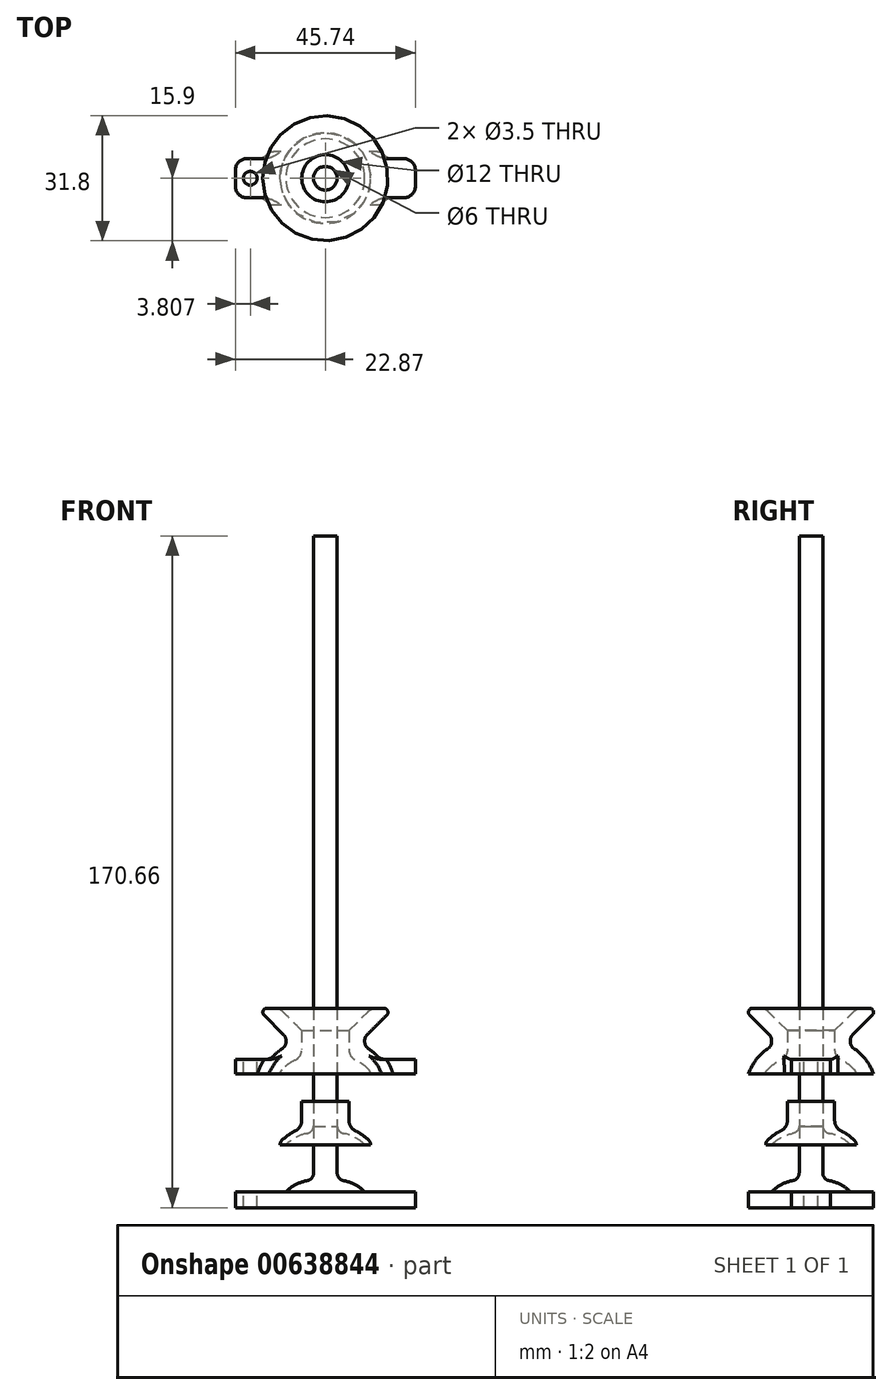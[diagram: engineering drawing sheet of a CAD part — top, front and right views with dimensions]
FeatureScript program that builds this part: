
annotation { "Feature Type Name" : "Feature", "Feature Type Description" : "" }
export const myFeature = defineFeature(function(context is Context, id is Id, definition is map)
    precondition{}
    {
        {
            var Q0;
            Q0=qCreatedBy(makeId("Front.planeOp"),FACE);
            var sketch = newSketch(context, id + "F0", { "sketchPlane" : qUnion([Q0])});
            skLineSegment(sketch, "E0", {"start": v(0, 0) * mm, "end": v(-3, 0) * mm, "construction": true});
            skLineSegment(sketch, "E1", {"start": v(-3, 1.83) * mm, "end": v(-3, 8) * mm});
            skPoint(sketch, "E2.endSnap0", {"position": v(-1.5, 0) * mm});
            skLineSegment(sketch, "E3", {"start": v(-3, 0) * mm, "end": v(-3, -3) * mm, "construction": true});
            skLineSegment(sketch, "E4", {"start": v(0, -3) * mm, "end": v(-10, -3) * mm, "construction": true});
            skArc(sketch, "E5", {"start": v(-4.66, -0.14) * mm, "mid": v(-7.56, -1.14) * mm, "end": v(-10, -3) * mm});
            skLineSegment(sketch, "E6", {"start": v(-3, 8) * mm, "end": v(-6, 8) * mm});
            skLineSegment(sketch, "E7", {"start": v(0, -3) * mm, "end": v(0, 8.98) * mm, "construction": true});
            skPoint(sketch, "E8.visualSharp", {"position": v(-11.5, -3) * mm});
            skPoint(sketch, "E9.visualSharp", {"position": v(-3, 0) * mm});
            skArc(sketch, "E9.filletArc", {"start": v(-4.66, -0.14) * mm, "mid": v(-3.47, 0.54) * mm, "end": v(-3, 1.83) * mm});
            skPoint(sketch, "E10.visualSharp", {"position": v(-10, -2.36) * mm});
            skArc(sketch, "E11.2", {"start": v(-7.73, 0.45) * mm, "mid": v(-9.52, -0.6) * mm, "end": v(-11.09, -1.97) * mm});
            skLineSegment(sketch, "E12", {"start": v(-6, 8) * mm, "end": v(-6, 3.17) * mm});
            skLineSegment(sketch, "E13", {"start": v(-10, -3) * mm, "end": v(-11.5, -3) * mm});
            skArc(sketch, "E14", {"start": v(-11.09, -1.97) * mm, "mid": v(-11.4, -2.44) * mm, "end": v(-11.5, -3) * mm});
            skPoint(sketch, "E15.visualSharp", {"position": v(-6, 1.09) * mm});
            skArc(sketch, "E15.filletArc", {"start": v(-7.73, 0.45) * mm, "mid": v(-6.47, 1.56) * mm, "end": v(-6, 3.17) * mm});
            skSolve(sketch);
        }
        {
            var Q0;
            Q0=makeQuery(id+"F0.imprint","IMPRINT",FACE,{"disambiguationData":[TD([[makeQuery(id+"F0.imprint","IMPRINT",EDGE,{"derivedFrom":sQuery(id+"F0.wireOp",EDGE,"E1")}),1.0]])]});
            var Q1;
            Q1=sQuery(id+"F0.wireOp",EDGE,"E7");
            revolve(context, id + "F1", {"entities" : qUnion([Q0]), "axis" : qUnion([Q1]), "revolveType" : RevolveType.FULL});
        }
        {
            var Q0;
            Q0=qCreatedBy(makeId("Front.planeOp"),FACE);
            var sketch = newSketch(context, id + "F2", { "sketchPlane" : qUnion([Q0])});
            skArc(sketch, "E16.0", {"start": v(-10.9, 3.44) * mm, "mid": v(-13.9, 0.63) * mm, "end": v(-15.84, -3) * mm});
            skLineSegment(sketch, "E16.1", {"start": v(-10, 5.51) * mm, "end": v(-10, 5.1) * mm});
            skLineSegment(sketch, "E17.0", {"start": v(-3, 1.83) * mm, "end": v(-3, 8) * mm});
            skArc(sketch, "E17.1", {"start": v(-4.66, -0.14) * mm, "mid": v(-7.56, -1.14) * mm, "end": v(-10, -3) * mm});
            skArc(sketch, "E18.0", {"start": v(-4.66, -0.14) * mm, "mid": v(-3.47, 0.54) * mm, "end": v(-3, 1.83) * mm});
            skLineSegment(sketch, "E19", {"start": v(-15.84, -3) * mm, "end": v(-15.84, -7) * mm});
            skLineSegment(sketch, "E20", {"start": v(-15.84, -7) * mm, "end": v(0, -7) * mm});
            skLineSegment(sketch, "E21", {"start": v(0, -7) * mm, "end": v(0, 8) * mm});
            skLineSegment(sketch, "E22", {"start": v(0, 8) * mm, "end": v(-3, 8) * mm});
            skLineSegment(sketch, "E23", {"start": v(-15.84, -3) * mm, "end": v(-15.84, 0.67) * mm, "construction": true});
            skLineSegment(sketch, "E24", {"start": v(-13.87, 0.67) * mm, "end": v(-25.87, 0.67) * mm});
            skLineSegment(sketch, "E25", {"start": v(-25.87, 0.67) * mm, "end": v(-25.87, -3) * mm});
            skLineSegment(sketch, "E26", {"start": v(-25.87, -3) * mm, "end": v(-15.84, -3) * mm});
            skLineSegment(sketch, "E27", {"start": v(-15.84, -7) * mm, "end": v(-25.87, -7) * mm});
            skLineSegment(sketch, "E28", {"start": v(-25.87, -7) * mm, "end": v(-25.87, -3) * mm});
            skLineSegment(sketch, "E29", {"start": v(-6, 8) * mm, "end": v(-11.66, 13.66) * mm});
            skLineSegment(sketch, "E30", {"start": v(-11.66, 13.66) * mm, "end": v(-17.31, 13.66) * mm});
            skLineSegment(sketch, "E31.trimOffspring", {"start": v(-10.59, 6.93) * mm, "end": v(-17.31, 13.66) * mm});
            skPoint(sketch, "E32.visualSharp", {"position": v(-10, 6.34) * mm});
            skArc(sketch, "E32.filletArc", {"start": v(-10, 5.51) * mm, "mid": v(-10.15, 6.28) * mm, "end": v(-10.59, 6.93) * mm});
            skPoint(sketch, "E33.visualSharp", {"position": v(-7.5, 3.98) * mm});
            skArc(sketch, "E33.filletArc", {"start": v(-10.9, 3.44) * mm, "mid": v(-10.24, 4.16) * mm, "end": v(-10, 5.1) * mm});
            skLineSegment(sketch, "E34", {"start": v(0, 8) * mm, "end": v(0, 13.66) * mm});
            skLineSegment(sketch, "E35", {"start": v(0, 13.66) * mm, "end": v(-3, 13.66) * mm});
            skLineSegment(sketch, "E36", {"start": v(-3, 13.66) * mm, "end": v(-3, 8) * mm});
            skArc(sketch, "E37.0", {"start": v(-11.09, -1.97) * mm, "mid": v(-11.4, -2.44) * mm, "end": v(-11.5, -3) * mm});
            skArc(sketch, "E37.1", {"start": v(-7.73, 0.45) * mm, "mid": v(-9.52, -0.6) * mm, "end": v(-11.09, -1.97) * mm});
            skArc(sketch, "E37.2", {"start": v(-7.73, 0.45) * mm, "mid": v(-6.47, 1.56) * mm, "end": v(-6, 3.17) * mm});
            skLineSegment(sketch, "E37.3", {"start": v(-6, 8) * mm, "end": v(-6, 3.17) * mm});
            skLineSegment(sketch, "E37.4", {"start": v(-10, -3) * mm, "end": v(-11.5, -3) * mm});
            skLineSegment(sketch, "E38", {"start": v(-11.5, -3) * mm, "end": v(-15.84, -3) * mm});
            skSolve(sketch);
        }
        {
            var Q0;
            Q0=makeQuery(id+"F2.imprint","IMPRINT",FACE,{"disambiguationData":[TD([[makeQuery(id+"F2.imprint","IMPRINT",EDGE,{"derivedFrom":sQuery(id+"F2.wireOp",EDGE,"E16.1")}),1.0]])]});
            var Q1;
            Q1=sQuery(id+"F0.wireOp",EDGE,"E7");
            revolve(context, id + "F3", {"surfaceOperationType" : NewSurfaceOperationType.NEW, "entities" : qUnion([Q0]), "axis" : qUnion([Q1]), "revolveType" : RevolveType.FULL});
        }
        {
            var Q0;
            Q0=makeQuery(id+"F2.imprint","IMPRINT",FACE,{"disambiguationData":[TD([[makeQuery(id+"F2.imprint","IMPRINT",EDGE,{"derivedFrom":sQuery(id+"F2.wireOp",EDGE,"E17.0")}),-1.0]])]});
            var Q1;
            Q1=makeQuery(id+"F2.imprint","IMPRINT",FACE,{"disambiguationData":[TD([[makeQuery(id+"F2.imprint","IMPRINT",EDGE,{"derivedFrom":sQuery(id+"F2.wireOp",EDGE,"E22")}),-1.0]])]});
            var Q2;
            Q2=sQuery(id+"F0.wireOp",EDGE,"E7");
            revolve(context, id + "F4", {"entities" : qUnion([Q0, Q1]), "axis" : qUnion([Q2]), "revolveType" : RevolveType.FULL});
        }
        {
            var Q0;
            {var subQ2=sQuery(id+"F2.wireOp",EDGE,"E24");Q0=makeQuery(id+"F2.imprint","IMPRINT",FACE,{"disambiguationData":[TD([[makeQuery(id+"F2.imprint","IMPRINT",EDGE,{"derivedFrom":subQ2}),1.0]])]});}
            extrude(context, id + "F5", {"entities" : qUnion([Q0]), "endBound" : BoundingType.SYMMETRIC, "depth" : 10 * mm, "offsetDistance" : 25 * mm});
        }
        {
            var Q0;
            Q0=makeQuery(id+"F2.imprint","IMPRINT",FACE,{"disambiguationData":[TD([[makeQuery(id+"F2.imprint","IMPRINT",EDGE,{"derivedFrom":sQuery(id+"F2.wireOp",EDGE,"E19")}),-1.0]])]});
            extrude(context, id + "F6", {"entities" : qUnion([Q0]), "endBound" : BoundingType.SYMMETRIC, "depth" : 10 * mm, "offsetDistance" : 25 * mm});
        }
        {
            var Q0;
            Q0=makeQuery(id+"F5.opExtrude","SWEPT_BODY",BODY,{"disambiguationData":[OSD([sQuery(id+"F2.wireOp",EDGE,"E16.0"),sQuery(id+"F2.wireOp",EDGE,"E24"),sQuery(id+"F2.wireOp",EDGE,"E25"),sQuery(id+"F2.wireOp",EDGE,"E26")])]});
            var Q1;
            Q1=makeQuery(id+"F6.opExtrude","SWEPT_BODY",BODY,{"disambiguationData":[OSD([sQuery(id+"F2.wireOp",EDGE,"E19"),sQuery(id+"F2.wireOp",EDGE,"E26"),sQuery(id+"F2.wireOp",EDGE,"E27"),sQuery(id+"F2.wireOp",EDGE,"E28")])]});
            transform(context, id + "F7", {"entities" : qUnion([Q0, Q1]), "transformType" : TransformType.TRANSLATION_3D, "dx" : 3 * mm, "dy" : 0 * mm, "dz" : 0 * mm, "makeCopy" : false});
        }
        {
            var Q0;
            Q0=makeQuery(id+"F5.opExtrude","SWEPT_BODY",BODY,{"disambiguationData":[OSD([sQuery(id+"F2.wireOp",EDGE,"E16.0"),sQuery(id+"F2.wireOp",EDGE,"E24"),sQuery(id+"F2.wireOp",EDGE,"E25"),sQuery(id+"F2.wireOp",EDGE,"E26")])]});
            var Q1;
            Q1=makeQuery(id+"F6.opExtrude","SWEPT_BODY",BODY,{"disambiguationData":[OSD([sQuery(id+"F2.wireOp",EDGE,"E19"),sQuery(id+"F2.wireOp",EDGE,"E26"),sQuery(id+"F2.wireOp",EDGE,"E27"),sQuery(id+"F2.wireOp",EDGE,"E28")])]});
            var Q2;
            Q2=qCreatedBy(makeId("Right.planeOp"),FACE);
            mirror(context, id + "F8", {"entities" : qUnion([Q0, Q1]), "mirrorPlane" : qUnion([Q2])});
        }
        {
            var Q0;
            Q0=makeQuery(id+"F5.opExtrude","SWEPT_BODY",BODY,{"disambiguationData":[OSD([sQuery(id+"F2.wireOp",EDGE,"E16.0"),sQuery(id+"F2.wireOp",EDGE,"E24"),sQuery(id+"F2.wireOp",EDGE,"E25"),sQuery(id+"F2.wireOp",EDGE,"E26")])]});
            var Q1;
            Q1=makeQuery(id+"F8.opPattern","COPY",BODY,{"derivedFrom":makeQuery(id+"F5.opExtrude","SWEPT_BODY",BODY,{"disambiguationData":[OSD([sQuery(id+"F2.wireOp",EDGE,"E16.0"),sQuery(id+"F2.wireOp",EDGE,"E24"),sQuery(id+"F2.wireOp",EDGE,"E25"),sQuery(id+"F2.wireOp",EDGE,"E26")])]}),"instanceName":"1"});
            var Q2;
            Q2=makeQuery(id+"F3.opRevolve","SWEPT_BODY",BODY,{"disambiguationData":[OSD([sQuery(id+"F2.wireOp",EDGE,"bc18d605-b98b-438b-80f2-28af09894532.0"),sQuery(id+"F2.wireOp",EDGE,"bc18d605-b98b-438b-80f2-28af09894532.1"),sQuery(id+"F2.wireOp",EDGE,"E16.0"),sQuery(id+"F2.wireOp",EDGE,"E16.1"),sQuery(id+"F2.wireOp",EDGE,"e265a185-1811-4eb8-86b9-4855075399bd.0"),sQuery(id+"F2.wireOp",EDGE,"0085ed8a-558a-43ff-81f7-92fb0c2dc086.0"),sQuery(id+"F2.wireOp",EDGE,"H8TFnSOD-seKw-8r3j-Luj8-icW1VKLXzKkm"),sQuery(id+"F2.wireOp",EDGE,"E29"),sQuery(id+"F2.wireOp",EDGE,"E30"),sQuery(id+"F2.wireOp",EDGE,"E31.trimOffspring"),sQuery(id+"F2.wireOp",EDGE,"E32.filletArc"),sQuery(id+"F2.wireOp",EDGE,"E33.filletArc")])]});
            booleanBodies(context, id + "F9", {"operationType" : BooleanOperationType.UNION, "tools" : qUnion([Q0, Q1, Q2])});
        }
        {
            var Q0;
            Q0=makeQuery(id+"F6.opExtrude","SWEPT_BODY",BODY,{"disambiguationData":[OSD([sQuery(id+"F2.wireOp",EDGE,"E19"),sQuery(id+"F2.wireOp",EDGE,"E26"),sQuery(id+"F2.wireOp",EDGE,"E27"),sQuery(id+"F2.wireOp",EDGE,"E28")])]});
            var Q1;
            Q1=makeQuery(id+"F4.opRevolve","SWEPT_BODY",BODY,{"disambiguationData":[OSD([sQuery(id+"F2.wireOp",EDGE,"E17.0"),sQuery(id+"F2.wireOp",EDGE,"E17.1"),sQuery(id+"F2.wireOp",EDGE,"E17.2"),sQuery(id+"F2.wireOp",EDGE,"E18.0"),sQuery(id+"F2.wireOp",EDGE,"H8TFnSOD-seKw-8r3j-Luj8-icW1VKLXzKkm"),sQuery(id+"F2.wireOp",EDGE,"E19"),sQuery(id+"F2.wireOp",EDGE,"E20"),sQuery(id+"F2.wireOp",EDGE,"E21"),sQuery(id+"F2.wireOp",EDGE,"E34"),sQuery(id+"F2.wireOp",EDGE,"E35"),sQuery(id+"F2.wireOp",EDGE,"E36")])]});
            var Q2;
            Q2=makeQuery(id+"F8.opPattern","COPY",BODY,{"derivedFrom":makeQuery(id+"F6.opExtrude","SWEPT_BODY",BODY,{"disambiguationData":[OSD([sQuery(id+"F2.wireOp",EDGE,"E19"),sQuery(id+"F2.wireOp",EDGE,"E26"),sQuery(id+"F2.wireOp",EDGE,"E27"),sQuery(id+"F2.wireOp",EDGE,"E28")])]}),"instanceName":"1"});
            booleanBodies(context, id + "F10", {"operationType" : BooleanOperationType.UNION, "tools" : qUnion([Q0, Q1, Q2])});
        }
        {
            var Q0;
            Q0=makeQuery(id+"F8.opPattern","COPY",EDGE,{"derivedFrom":makeQuery(id+"F5.opExtrude","CAP_EDGE",EDGE,{"disambiguationData":[OSD([sQuery(id+"F2.wireOp",EDGE,"E25")])],"isStart":false}),"instanceName":"1"});
            var Q1;
            Q1=makeQuery(id+"F8.opPattern","COPY",EDGE,{"derivedFrom":makeQuery(id+"F5.opExtrude","CAP_EDGE",EDGE,{"disambiguationData":[OSD([sQuery(id+"F2.wireOp",EDGE,"E25")])],"isStart":true}),"instanceName":"1"});
            var Q2;
            Q2=makeQuery(id+"F8.opPattern","COPY",EDGE,{"derivedFrom":makeQuery(id+"F6.opExtrude","CAP_EDGE",EDGE,{"disambiguationData":[OSD([sQuery(id+"F2.wireOp",EDGE,"E28")])],"isStart":true}),"instanceName":"1"});
            var Q3;
            Q3=makeQuery(id+"F8.opPattern","COPY",EDGE,{"derivedFrom":makeQuery(id+"F6.opExtrude","CAP_EDGE",EDGE,{"disambiguationData":[OSD([sQuery(id+"F2.wireOp",EDGE,"E28")])],"isStart":false}),"instanceName":"1"});
            var Q4;
            {var subQ0=sQuery(id+"F2.wireOp",EDGE,"E19");Q4=makeQuery(id+"F10.opBoolean","INTERSECT",EDGE,{"derivedFrom":[makeQuery(id+"F4.opRevolve","SWEPT_FACE",FACE,{"disambiguationData":[OSD([subQ0])]}),makeQuery(id+"F8.opPattern","COPY",FACE,{"derivedFrom":makeQuery(id+"F6.opExtrude","CAP_FACE",FACE,{"disambiguationData":[OSD([subQ0,sQuery(id+"F2.wireOp",EDGE,"E26"),sQuery(id+"F2.wireOp",EDGE,"E27"),sQuery(id+"F2.wireOp",EDGE,"E28")])],"isStart":false}),"instanceName":"1"})]});}
            var Q5;
            {var subQ0=sQuery(id+"F2.wireOp",EDGE,"E19");Q5=makeQuery(id+"F10.opBoolean","INTERSECT",EDGE,{"derivedFrom":[makeQuery(id+"F4.opRevolve","SWEPT_FACE",FACE,{"disambiguationData":[OSD([subQ0])]}),makeQuery(id+"F8.opPattern","COPY",FACE,{"derivedFrom":makeQuery(id+"F6.opExtrude","CAP_FACE",FACE,{"disambiguationData":[OSD([subQ0,sQuery(id+"F2.wireOp",EDGE,"E26"),sQuery(id+"F2.wireOp",EDGE,"E27"),sQuery(id+"F2.wireOp",EDGE,"E28")])],"isStart":true}),"instanceName":"1"})]});}
            var Q6;
            {var subQ0=sQuery(id+"F2.wireOp",EDGE,"E19");Q6=makeQuery(id+"F10.opBoolean","INTERSECT",EDGE,{"derivedFrom":[makeQuery(id+"F4.opRevolve","SWEPT_FACE",FACE,{"disambiguationData":[OSD([subQ0])]}),makeQuery(id+"F6.opExtrude","CAP_FACE",FACE,{"disambiguationData":[OSD([subQ0,sQuery(id+"F2.wireOp",EDGE,"E26"),sQuery(id+"F2.wireOp",EDGE,"E27"),sQuery(id+"F2.wireOp",EDGE,"E28")])],"isStart":false})]});}
            var Q7;
            Q7=makeQuery(id+"F6.opExtrude","CAP_EDGE",EDGE,{"disambiguationData":[OSD([sQuery(id+"F2.wireOp",EDGE,"E28")])],"isStart":false});
            var Q8;
            Q8=makeQuery(id+"F5.opExtrude","CAP_EDGE",EDGE,{"disambiguationData":[OSD([sQuery(id+"F2.wireOp",EDGE,"E25")])],"isStart":false});
            var Q9;
            Q9=makeQuery(id+"F5.opExtrude","CAP_EDGE",EDGE,{"disambiguationData":[OSD([sQuery(id+"F2.wireOp",EDGE,"E25")])],"isStart":true});
            var Q10;
            Q10=makeQuery(id+"F6.opExtrude","CAP_EDGE",EDGE,{"disambiguationData":[OSD([sQuery(id+"F2.wireOp",EDGE,"E28")])],"isStart":true});
            var Q11;
            {var subQ0=sQuery(id+"F2.wireOp",EDGE,"E19");Q11=makeQuery(id+"F10.opBoolean","INTERSECT",EDGE,{"derivedFrom":[makeQuery(id+"F4.opRevolve","SWEPT_FACE",FACE,{"disambiguationData":[OSD([subQ0])]}),makeQuery(id+"F6.opExtrude","CAP_FACE",FACE,{"disambiguationData":[OSD([subQ0,sQuery(id+"F2.wireOp",EDGE,"E26"),sQuery(id+"F2.wireOp",EDGE,"E27"),sQuery(id+"F2.wireOp",EDGE,"E28")])],"isStart":true})]});}
            var Q12;
            {var subQ0=sQuery(id+"F2.wireOp",EDGE,"E16.0");Q12=makeQuery(id+"F9.opBoolean","INTERSECT",EDGE,{"derivedFrom":[makeQuery(id+"F3.opRevolve","SWEPT_FACE",FACE,{"disambiguationData":[OSD([subQ0])]}),makeQuery(id+"F5.opExtrude","CAP_FACE",FACE,{"disambiguationData":[OSD([subQ0,sQuery(id+"F2.wireOp",EDGE,"E24"),sQuery(id+"F2.wireOp",EDGE,"E25"),sQuery(id+"F2.wireOp",EDGE,"E26")])],"isStart":true})]});}
            var Q13;
            {var subQ0=sQuery(id+"F2.wireOp",EDGE,"E16.0");Q13=makeQuery(id+"F9.opBoolean","INTERSECT",EDGE,{"derivedFrom":[makeQuery(id+"F3.opRevolve","SWEPT_FACE",FACE,{"disambiguationData":[OSD([subQ0])]}),makeQuery(id+"F5.opExtrude","CAP_FACE",FACE,{"disambiguationData":[OSD([subQ0,sQuery(id+"F2.wireOp",EDGE,"E24"),sQuery(id+"F2.wireOp",EDGE,"E25"),sQuery(id+"F2.wireOp",EDGE,"E26")])],"isStart":false})]});}
            var Q14;
            {var subQ0=sQuery(id+"F2.wireOp",EDGE,"E16.0");Q14=makeQuery(id+"F9.opBoolean","INTERSECT",EDGE,{"derivedFrom":[makeQuery(id+"F3.opRevolve","SWEPT_FACE",FACE,{"disambiguationData":[OSD([subQ0])]}),makeQuery(id+"F8.opPattern","COPY",FACE,{"derivedFrom":makeQuery(id+"F5.opExtrude","CAP_FACE",FACE,{"disambiguationData":[OSD([subQ0,sQuery(id+"F2.wireOp",EDGE,"E24"),sQuery(id+"F2.wireOp",EDGE,"E25"),sQuery(id+"F2.wireOp",EDGE,"E26")])],"isStart":false}),"instanceName":"1"})]});}
            var Q15;
            {var subQ0=sQuery(id+"F2.wireOp",EDGE,"E16.0");Q15=makeQuery(id+"F9.opBoolean","INTERSECT",EDGE,{"derivedFrom":[makeQuery(id+"F3.opRevolve","SWEPT_FACE",FACE,{"disambiguationData":[OSD([subQ0])]}),makeQuery(id+"F8.opPattern","COPY",FACE,{"derivedFrom":makeQuery(id+"F5.opExtrude","CAP_FACE",FACE,{"disambiguationData":[OSD([subQ0,sQuery(id+"F2.wireOp",EDGE,"E24"),sQuery(id+"F2.wireOp",EDGE,"E25"),sQuery(id+"F2.wireOp",EDGE,"E26")])],"isStart":true}),"instanceName":"1"})]});}
            var Q16;
            Q16=makeQuery(id+"F9.opBoolean","INTERSECT",EDGE,{"derivedFrom":[makeQuery(id+"F3.opRevolve","SWEPT_FACE",FACE,{"disambiguationData":[OSD([sQuery(id+"F2.wireOp",EDGE,"E16.0")])]}),makeQuery(id+"F8.opPattern","COPY",FACE,{"derivedFrom":makeQuery(id+"F5.opExtrude","SWEPT_FACE",FACE,{"disambiguationData":[OSD([sQuery(id+"F2.wireOp",EDGE,"E24")])]}),"instanceName":"1"})]});
            var Q17;
            Q17=makeQuery(id+"F9.opBoolean","INTERSECT",EDGE,{"derivedFrom":[makeQuery(id+"F3.opRevolve","SWEPT_FACE",FACE,{"disambiguationData":[OSD([sQuery(id+"F2.wireOp",EDGE,"E16.0")])]}),makeQuery(id+"F5.opExtrude","SWEPT_FACE",FACE,{"disambiguationData":[OSD([sQuery(id+"F2.wireOp",EDGE,"E24")])]})]});
            var Q18;
            Q18=makeQuery(id+"F3.opRevolve","SWEPT_EDGE",EDGE,{"disambiguationData":[OSD([sQuery(id+"F2.wireOp",EDGE,"E29"),sQuery(id+"F2.wireOp",EDGE,"E30")])]});
            fillet(context, id + "F11", {"entities" : qUnion([Q0, Q1, Q2, Q3, Q4, Q5, Q6, Q7, Q8, Q9, Q10, Q11, Q12, Q13, Q14, Q15, Q16, Q17, Q18]), "radius" : 3 * mm, "tangentPropagation" : true, "allowEdgeOverflow" : false});
        }
        {
            var Q0;
            Q0=makeQuery(id+"F3.opRevolve","SWEPT_EDGE",EDGE,{"disambiguationData":[OSD([sQuery(id+"F2.wireOp",EDGE,"E30"),sQuery(id+"F2.wireOp",EDGE,"E31.trimOffspring")])]});
            fillet(context, id + "F12", {"entities" : qUnion([Q0]), "radius" : 1 * mm, "tangentPropagation" : true, "allowEdgeOverflow" : false});
        }
        {
            var Q0;
            Q0=makeQuery(id+"F5.opExtrude","SWEPT_FACE",FACE,{"disambiguationData":[OSD([sQuery(id+"F2.wireOp",EDGE,"E24")])]});
            var sketch = newSketch(context, id + "F13", { "sketchPlane" : qUnion([Q0])});
            skLineSegment(sketch, "E39", {"start": v(-15.25, 0) * mm, "end": v(-22.87, 0) * mm, "construction": true});
            skCircle(sketch, "E40", {"center": v(-19.06, 0) * mm, "radius": 1.75 * mm});
            skLineSegment(sketch, "E41", {"start": v(0, 0) * mm, "end": v(0, 16.55) * mm, "construction": true});
            skCircle(sketch, "E42.MirrorC", {"center": v(19.06, 0) * mm, "radius": 1.75 * mm});
            skSolve(sketch);
        }
        {
            var Q0;
            Q0=makeQuery(id+"F13.imprint","IMPRINT",FACE,{"disambiguationData":[TD([[makeQuery(id+"F13.imprint","IMPRINT",EDGE,{"derivedFrom":sQuery(id+"F13.wireOp",EDGE,"E40")}),1.0]])]});
            var Q1;
            Q1=makeQuery(id+"F13.imprint","IMPRINT",FACE,{"disambiguationData":[TD([[makeQuery(id+"F13.imprint","IMPRINT",EDGE,{"derivedFrom":sQuery(id+"F13.wireOp",EDGE,"E42.MirrorC")}),-1.0]])]});
            extrude(context, id + "F14", {"entities" : qUnion([Q0, Q1]), "operationType" : NewBodyOperationType.REMOVE, "oppositeDirection" : true, "depth" : 25 * mm, "offsetDistance" : 25 * mm});
        }
        {
            var Q0;
            Q0=makeQuery(id+"F6.opExtrude","SWEPT_BODY",BODY,{"disambiguationData":[OSD([sQuery(id+"F2.wireOp",EDGE,"E19"),sQuery(id+"F2.wireOp",EDGE,"E26"),sQuery(id+"F2.wireOp",EDGE,"E27"),sQuery(id+"F2.wireOp",EDGE,"E28")])]});
            transform(context, id + "F15", {"entities" : qUnion([Q0]), "transformType" : TransformType.TRANSLATION_3D, "dx" : 0 * mm, "dy" : 0 * mm, "dz" : -30 * mm, "makeCopy" : false});
        }
        {
            var Q0;
            Q0=makeQuery(id+"F1.opRevolve","SWEPT_BODY",BODY,{"disambiguationData":[OSD([sQuery(id+"F0.wireOp",EDGE,"E1"),sQuery(id+"F0.wireOp",EDGE,"E5"),sQuery(id+"F0.wireOp",EDGE,"E6"),sQuery(id+"F0.wireOp",EDGE,"E9.filletArc"),sQuery(id+"F0.wireOp",EDGE,"E11.2"),sQuery(id+"F0.wireOp",EDGE,"E12"),sQuery(id+"F0.wireOp",EDGE,"E13"),sQuery(id+"F0.wireOp",EDGE,"E14"),sQuery(id+"F0.wireOp",EDGE,"E15.filletArc")])]});
            transform(context, id + "F16", {"entities" : qUnion([Q0]), "transformType" : TransformType.TRANSLATION_3D, "dx" : 0 * mm, "dy" : 0 * mm, "dz" : -18 * mm, "makeCopy" : false});
        }
        {
            var Q0;
            Q0=makeQuery(id+"F4.opRevolve","SWEPT_FACE",FACE,{"disambiguationData":[OSD([sQuery(id+"F2.wireOp",EDGE,"E35")])]});
            extrude(context, id + "F17", {"entities" : qUnion([Q0]), "depth" : 150 * mm, "offsetDistance" : 25 * mm});
        }
    });
